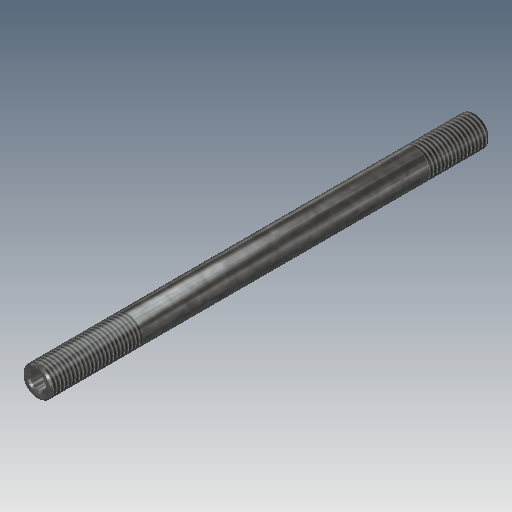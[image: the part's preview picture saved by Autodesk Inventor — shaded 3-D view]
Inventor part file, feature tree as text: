
AUTODESK INVENTOR PART (.ipt)
format: ipt  version: 2018 (Build 220112000, 112)  size: 136,704 bytes
history: native  units: mm
features: thread x2, extrude x1, plane x1, chamfer x1, sketch x1
ambient origin geometry x8: Origin, YZ Plane, XZ Plane, XY Plane, X Axis, Y Axis, Z Axis, Center Point
bodies: Solid1 (feature_tree)
feature tree (6):
  extrude  "Extrusion1"  Depth=145.4mm
  thread  "Thread1"  [1 undecoded]
  plane  "Work Plane1"
  thread  "Thread2"  [1 undecoded]
  chamfer  "Chamfer2"  Distance=30.0mm
  sketch  "Sketch1"  dims[d0=9.86mm d1=5.12mm d2=145.4mm d3=0.0mm d4=20.0mm d5=0.0mm d9=30.0mm d10=0.0mm d11=0.5mm d12=2.0mm d13=45.0deg]
note: 2 required parameter values undecoded (feature->parameter linkage not recoverable at this tier; creation-order binding heuristic only, values carry confidence <= 0.55)
